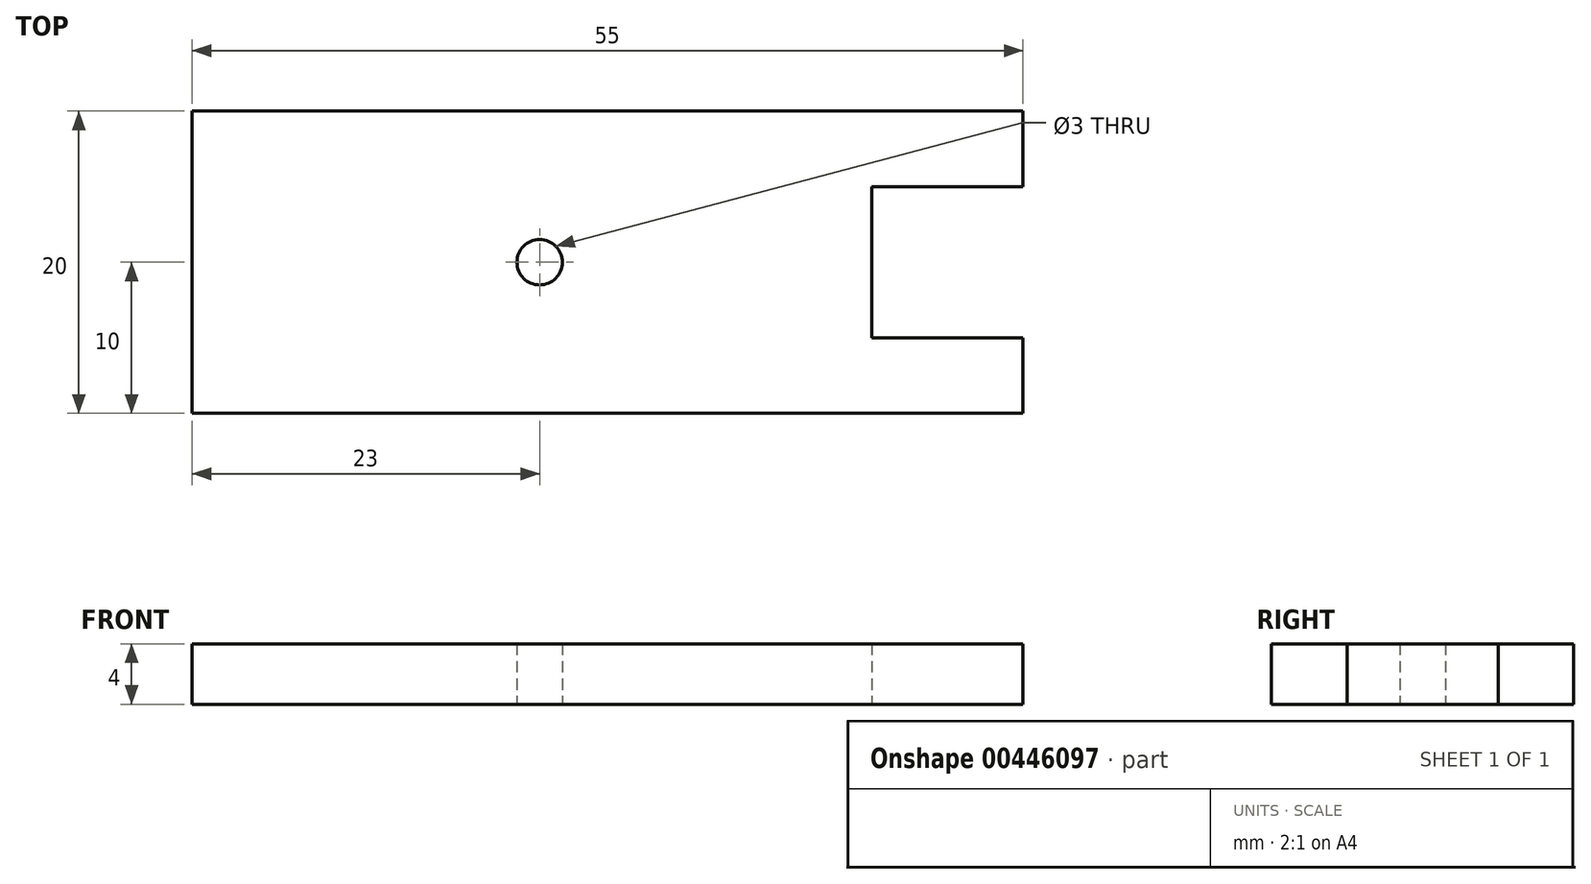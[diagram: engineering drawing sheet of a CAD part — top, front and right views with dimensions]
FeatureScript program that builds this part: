
annotation { "Feature Type Name" : "Feature", "Feature Type Description" : "" }
export const myFeature = defineFeature(function(context is Context, id is Id, definition is map)
    precondition{}
    {
        {
            var Q0;
            Q0=qCreatedBy(makeId("Top.planeOp"),FACE);
            var sketch = newSketch(context, id + "F0", { "sketchPlane" : qUnion([Q0])});
            skCircle(sketch, "E0", {"center": v(0, 0) * mm, "radius": 1.5 * mm});
            skLineSegment(sketch, "E1", {"start": v(-23, 0) * mm, "end": v(-23, 10) * mm});
            skLineSegment(sketch, "E2", {"start": v(-23, 10) * mm, "end": v(32, 10) * mm});
            skLineSegment(sketch, "E3", {"start": v(32, 10) * mm, "end": v(32, 5) * mm});
            skLineSegment(sketch, "E4", {"start": v(32, 5) * mm, "end": v(22, 5) * mm});
            skLineSegment(sketch, "E5", {"start": v(22, 5) * mm, "end": v(22, 0) * mm});
            skLineSegment(sketch, "E6.MirrorCS", {"start": v(-23, -10) * mm, "end": v(32, -10) * mm});
            skLineSegment(sketch, "E7.MirrorCS", {"start": v(-23, 0) * mm, "end": v(-23, -10) * mm});
            skLineSegment(sketch, "E8.MirrorCS", {"start": v(32, -10) * mm, "end": v(32, -5) * mm});
            skLineSegment(sketch, "E9.MirrorCS", {"start": v(32, -5) * mm, "end": v(22, -5) * mm});
            skLineSegment(sketch, "E10.MirrorCS", {"start": v(22, -5) * mm, "end": v(22, 0) * mm});
            skSolve(sketch);
        }
        {
            var Q0;
            Q0 = qSketchRegion(id + "F0", true);
            extrude(context, id + "F1", {"entities" : qUnion([Q0]), "depth" : 4 * mm, "offsetDistance" : 25 * mm});
        }
    });
